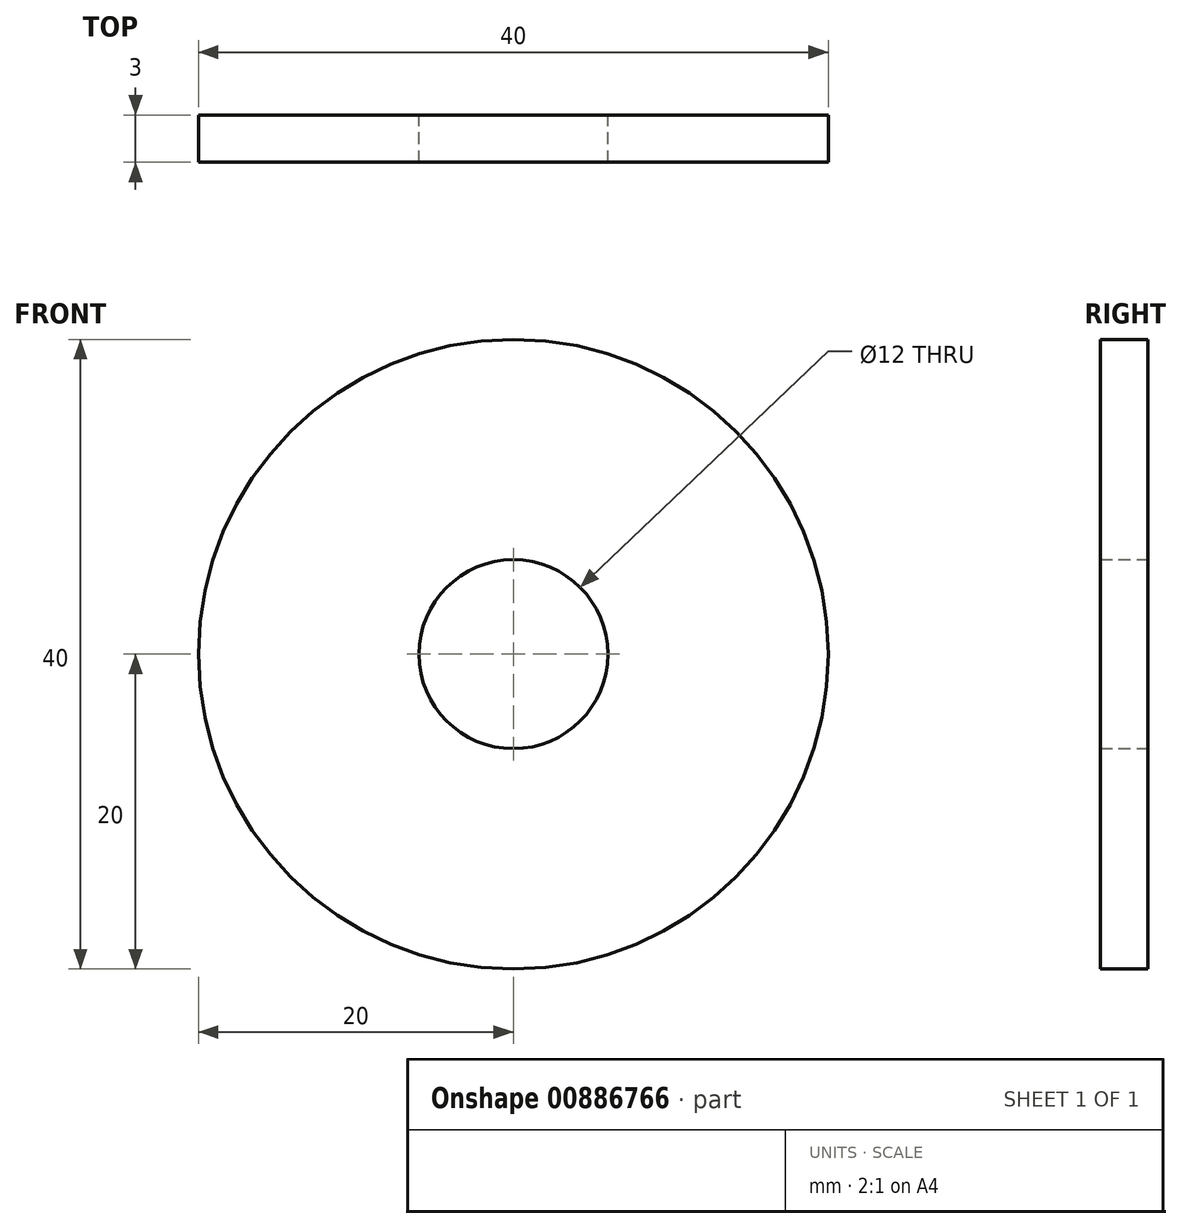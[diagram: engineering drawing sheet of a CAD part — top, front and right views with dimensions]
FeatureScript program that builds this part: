
annotation { "Feature Type Name" : "Feature", "Feature Type Description" : "" }
export const myFeature = defineFeature(function(context is Context, id is Id, definition is map)
    precondition{}
    {
        {
            var Q0;
            Q0=qCreatedBy(makeId("Front.planeOp"),FACE);
            var sketch = newSketch(context, id + "F0", { "sketchPlane" : qUnion([Q0])});
            skCircle(sketch, "E0", {"center": v(0, 0) * mm, "radius": 20 * mm});
            skCircle(sketch, "E1", {"center": v(0, 0) * mm, "radius": 6 * mm});
            skSolve(sketch);
        }
        {
            var Q0;
            Q0 = qSketchRegion(id + "F0", true);
            extrude(context, id + "F1", {"entities" : qUnion([Q0]), "depth" : 3 * mm, "offsetDistance" : 25 * mm});
        }
    });
